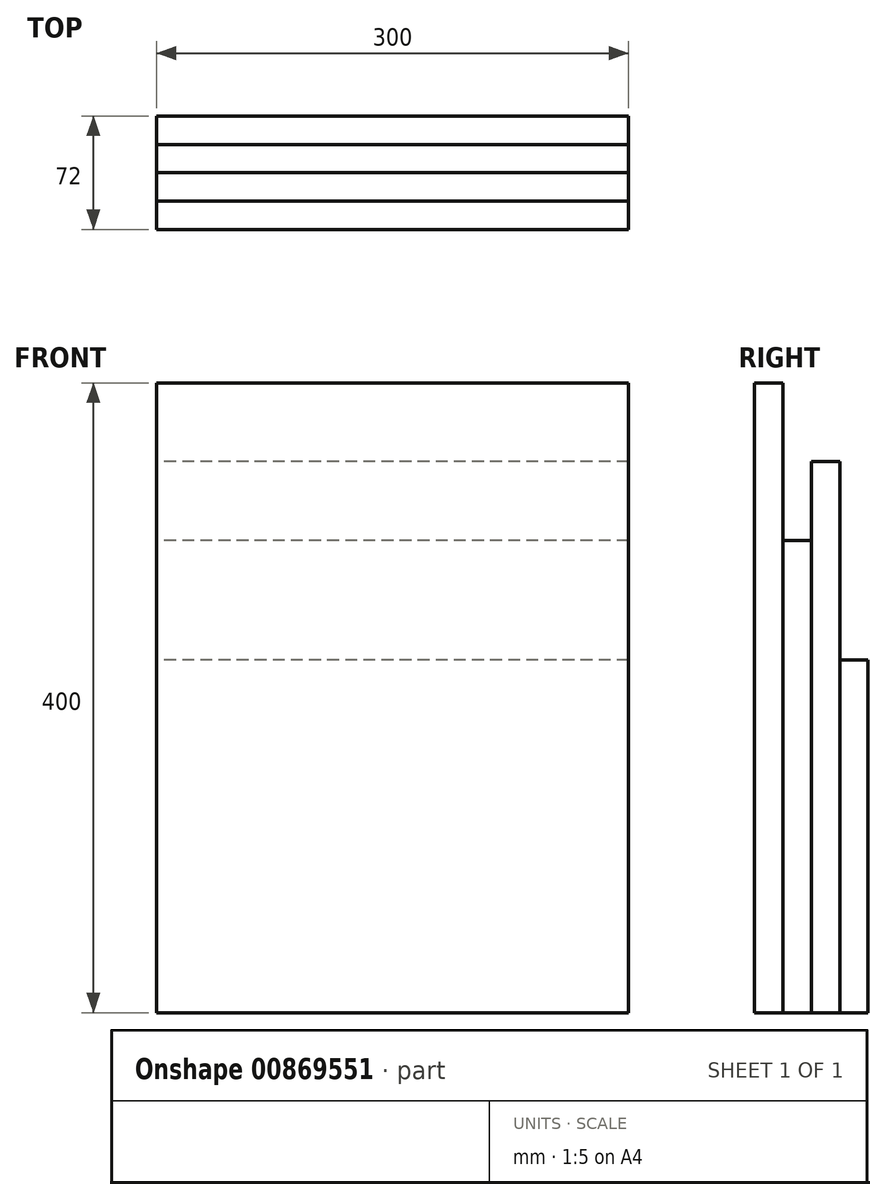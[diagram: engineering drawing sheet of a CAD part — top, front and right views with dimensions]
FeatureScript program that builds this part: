
annotation { "Feature Type Name" : "Feature", "Feature Type Description" : "" }
export const myFeature = defineFeature(function(context is Context, id is Id, definition is map)
    precondition{}
    {
        {
            var Q0;
            Q0=qCreatedBy(makeId("Front.planeOp"),FACE);
            var sketch = newSketch(context, id + "F0", { "sketchPlane" : qUnion([Q0])});
            skLineSegment(sketch, "E0.bottom", {"start": v(0, 0) * mm, "end": v(300, 0) * mm});
            skLineSegment(sketch, "E0.top", {"start": v(0, -400) * mm, "end": v(300, -400) * mm});
            skLineSegment(sketch, "E0.left", {"start": v(0, 0) * mm, "end": v(0, -400) * mm});
            skLineSegment(sketch, "E0.right", {"start": v(300, 0) * mm, "end": v(300, -400) * mm});
            skSolve(sketch);
        }
        {
            var Q0;
            Q0 = qSketchRegion(id + "F0", true);
            extrude(context, id + "F1", {"entities" : qUnion([Q0]), "oppositeDirection" : true, "depth" : 18 * mm, "offsetDistance" : 25 * mm});
        }
        {
            var Q0;
            Q0=makeQuery(id+"F1.opExtrude","CAP_FACE",FACE,{"disambiguationData":[OSD([sQuery(id+"F0.wireOp",EDGE,"E0.bottom"),sQuery(id+"F0.wireOp",EDGE,"E0.top"),sQuery(id+"F0.wireOp",EDGE,"E0.left"),sQuery(id+"F0.wireOp",EDGE,"E0.right")])],"isStart":false});
            var sketch = newSketch(context, id + "F2", { "sketchPlane" : qUnion([Q0])});
            skLineSegment(sketch, "E1.bottom", {"start": v(-300, -400) * mm, "end": v(0, -400) * mm});
            skLineSegment(sketch, "E1.top", {"start": v(-300, -100) * mm, "end": v(0, -100) * mm});
            skLineSegment(sketch, "E1.left", {"start": v(-300, -400) * mm, "end": v(-300, -100) * mm});
            skLineSegment(sketch, "E1.right", {"start": v(0, -400) * mm, "end": v(0, -100) * mm});
            skSolve(sketch);
        }
        {
            var Q0;
            Q0 = qSketchRegion(id + "F2", true);
            extrude(context, id + "F3", {"entities" : qUnion([Q0]), "depth" : 18 * mm, "offsetDistance" : 25 * mm});
        }
        {
            var Q0;
            Q0=makeQuery(id+"F3.opExtrude","CAP_FACE",FACE,{"disambiguationData":[OSD([sQuery(id+"F2.wireOp",EDGE,"E1.bottom"),sQuery(id+"F2.wireOp",EDGE,"E1.top"),sQuery(id+"F2.wireOp",EDGE,"E1.left"),sQuery(id+"F2.wireOp",EDGE,"E1.right")])],"isStart":false});
            var sketch = newSketch(context, id + "F4", { "sketchPlane" : qUnion([Q0])});
            skLineSegment(sketch, "E2.bottom", {"start": v(-300, -400) * mm, "end": v(0, -400) * mm});
            skLineSegment(sketch, "E2.top", {"start": v(-300, -50) * mm, "end": v(0, -50) * mm});
            skLineSegment(sketch, "E2.left", {"start": v(-300, -400) * mm, "end": v(-300, -50) * mm});
            skLineSegment(sketch, "E2.right", {"start": v(0, -400) * mm, "end": v(0, -50) * mm});
            skSolve(sketch);
        }
        {
            var Q0;
            Q0 = qSketchRegion(id + "F4", true);
            extrude(context, id + "F5", {"entities" : qUnion([Q0]), "depth" : 18 * mm, "offsetDistance" : 25 * mm});
        }
        {
            var Q0;
            Q0=makeQuery(id+"F5.opExtrude","CAP_FACE",FACE,{"disambiguationData":[OSD([sQuery(id+"F4.wireOp",EDGE,"E2.bottom"),sQuery(id+"F4.wireOp",EDGE,"E2.top"),sQuery(id+"F4.wireOp",EDGE,"E2.left"),sQuery(id+"F4.wireOp",EDGE,"E2.right")])],"isStart":false});
            var sketch = newSketch(context, id + "F6", { "sketchPlane" : qUnion([Q0])});
            skLineSegment(sketch, "E3.bottom", {"start": v(-300, -400) * mm, "end": v(0, -400) * mm});
            skLineSegment(sketch, "E3.top", {"start": v(-300, -176) * mm, "end": v(0, -176) * mm});
            skLineSegment(sketch, "E3.left", {"start": v(-300, -400) * mm, "end": v(-300, -176) * mm});
            skLineSegment(sketch, "E3.right", {"start": v(0, -400) * mm, "end": v(0, -176) * mm});
            skSolve(sketch);
        }
        {
            var Q0;
            Q0 = qSketchRegion(id + "F6", true);
            extrude(context, id + "F7", {"entities" : qUnion([Q0]), "depth" : 18 * mm, "offsetDistance" : 25 * mm});
        }
    });
